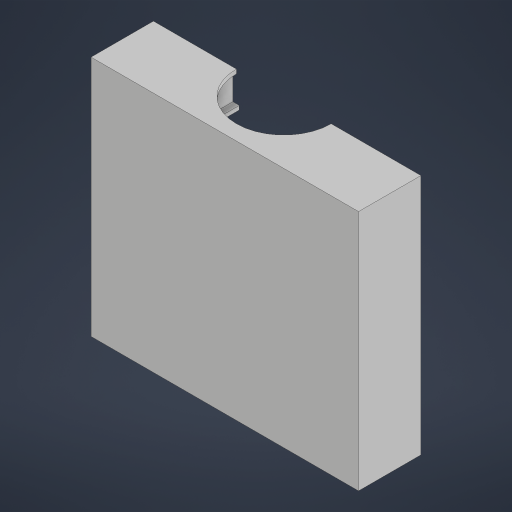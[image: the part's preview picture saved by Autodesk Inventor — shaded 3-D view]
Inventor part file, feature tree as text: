
AUTODESK INVENTOR PART (.ipt)
format: ipt  version: 2023 (Build 270158000, 158)  size: 336,896 bytes
history: native  units: in
note: dims shown in document units (in); Inventor stores cm internally (conversion verified against a paired STEP export)
features: extrude x12, sketch x12, reference x11, other x5, plane x3, projected_geometry x2
ambient origin geometry x8: Origin, YZ Plane, XZ Plane, XY Plane, X Axis, Y Axis, Z Axis, Center Point
bodies: Solid1 (feature_tree)
feature tree (45):
  plane  "Work Plane1"
  extrude  "Extrusion1"  Depth=0.04in
  extrude  "Extrusion2"  Depth=0.5512in
  extrude  "Extrusion3"  Depth=0.065in
  extrude  "Extrusion4"  TaperAngle=0.0deg  [1 undecoded]
  extrude  "Extrusion5"  Depth=0.7874in TaperAngle=0.0deg
  extrude  "Extrusion6"  Depth=0.1969in TaperAngle=0.0deg
  sketch  "Sketch7"  dims[d16=0.05in d17=0.1181in d18=0.0in]
  plane  "Work Plane2"
  extrude  "Extrusion7"  Depth=0.1181in TaperAngle=0.0deg
  extrude  "Extrusion8"  Depth=0.1181in TaperAngle=0.0deg
  extrude  "Extrusion9"  Depth=0.1181in TaperAngle=0.0deg
  sketch  "Sketch10"  dims[d28=1.7853in d29=0.05in]
  plane  "Work Plane3"
  extrude  "Extrusion10"  Depth=0.05in
  extrude  "Extrusion11"  Depth=0.05in
  extrude  "Extrusion12"  Depth=0.1in
  sketch  "Sketch1"  dims[d0=0.04in d1=0.04in]
  reference  "Reference1"
  reference  "Reference2"
  sketch  "Sketch2"  dims[d2=0.5512in d3=0.5512in]
  projected_geometry  "Projected Loop1"
  sketch  "Sketch3"  dims[d5=0.065in d6=0.065in]
  sketch  "Sketch4"  dims[d7=0.065in d8=0.0in]
  reference  "Reference3"
  reference  "Reference4"
  reference  "Reference5"
  reference  "Reference6"
  sketch  "Sketch5"  dims[d9=0.065in d10=0.7874in d11=0.0in]
  reference  "Reference7"
  reference  "Reference8"
  reference  "Reference9"
  sketch  "Sketch6"  dims[d12=0.1969in d13=0.0in d14=0.0787in d15=0.0in]
  reference  "Reference10"
  reference  "Reference11"
  sketch  "Sketch8"  dims[d19=0.6378in d22=0.1181in d23=0.0in]
  projected_geometry  "Projected Loop2"
  sketch  "Sketch9"  dims[d24=0.05in d25=0.1181in d26=0.0in]
  sketch  "Sketch11"  dims[d30=0.15in d31=0.05in]
  sketch  "Sketch12"  dims[d32=1.7323in d33=0.8661in d34=0.4724in d35=1.0in d36=0.0in d45=1.0in d46=0.0in d47=0.1in d48=0.1in d49=0.063in d50=0.063in d51=0.063in d52=0.063in d53=1.4961in d54=1.0in d55=0.0in d56=0.4724in d57=1.7323in d58=0.8661in d59=1.0in d60=0.0in d62=0.063in d63=0.1in d64=0.063in d65=0.063in d66=0.063in d67=0.1in d68=1.0in d69=0.0in d70=1.4961in d71=1.0in d72=0.0in]
  other  "<userpath>\Documents\Inventor\2024 Mavericks\Orange PI\OrangePICover.iam"
  other  "OrangePICover.iam"
  other  "OPi5_pcb_asm-0809:1"
  other  "orangepicover-002:1"
  other  "Assembly10"
note: 1 required parameter value undecoded (feature->parameter linkage not recoverable at this tier; creation-order binding heuristic only, values carry confidence <= 0.55)
